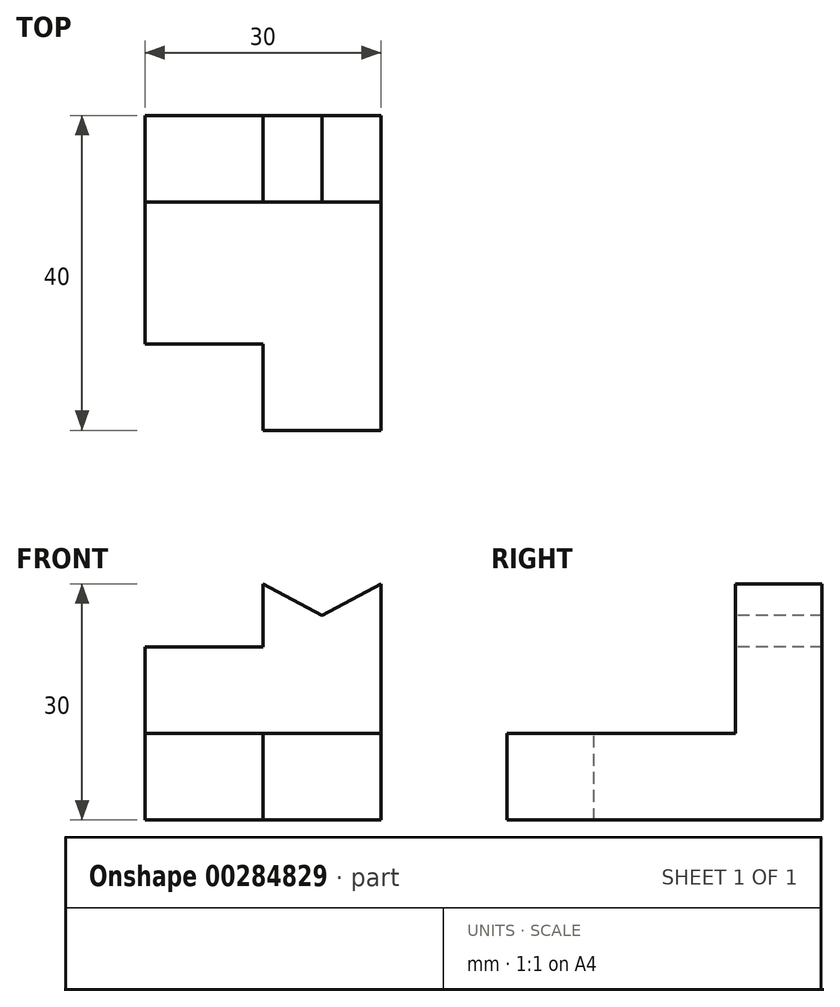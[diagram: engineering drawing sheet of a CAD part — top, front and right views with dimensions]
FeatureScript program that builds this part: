
annotation { "Feature Type Name" : "Feature", "Feature Type Description" : "" }
export const myFeature = defineFeature(function(context is Context, id is Id, definition is map)
    precondition{}
    {
        {
            var Q0;
            Q0=qCreatedBy(makeId("Front.planeOp"),FACE);
            var sketch = newSketch(context, id + "F0", { "sketchPlane" : qUnion([Q0])});
            skLineSegment(sketch, "E0.bottom", {"start": v(0, 0) * mm, "end": v(40, 0) * mm});
            skLineSegment(sketch, "E0.top", {"start": v(0, 30) * mm, "end": v(40, 30) * mm});
            skLineSegment(sketch, "E0.left", {"start": v(0, 0) * mm, "end": v(0, 30) * mm});
            skLineSegment(sketch, "E0.right", {"start": v(40, 0) * mm, "end": v(40, 30) * mm});
            skLineSegment(sketch, "E1.bottom", {"start": v(40, 30) * mm, "end": v(11, 30) * mm});
            skLineSegment(sketch, "E1.top", {"start": v(40, 11) * mm, "end": v(11, 11) * mm});
            skLineSegment(sketch, "E1.left", {"start": v(40, 30) * mm, "end": v(40, 11) * mm});
            skLineSegment(sketch, "E1.right", {"start": v(11, 30) * mm, "end": v(11, 11) * mm});
            skSolve(sketch);
        }
        {
            var Q0;
            Q0=makeQuery(id+"F0.imprint","IMPRINT",FACE,{"disambiguationData":[TD([[makeQuery(id+"F0.imprint","IMPRINT",EDGE,{"derivedFrom":sQuery(id+"F0.wireOp",EDGE,"E0.bottom")}),1.0]])]});
            extrude(context, id + "F1", {"entities" : qUnion([Q0]), "depth" : 30 * mm});
        }
        {
            var Q0;
            Q0=makeQuery(id+"F1.opExtrude","SWEPT_FACE",FACE,{"disambiguationData":[OSD([sQuery(id+"F0.wireOp",EDGE,"E1.top")])]});
            var sketch = newSketch(context, id + "F2", { "sketchPlane" : qUnion([Q0])});
            skPoint(sketch, "E2.oppositeSnap0", {"position": v(40, -15) * mm});
            skLineSegment(sketch, "E2.bottom", {"start": v(40, -30) * mm, "end": v(29, -30) * mm});
            skLineSegment(sketch, "E2.top", {"start": v(40, -15) * mm, "end": v(29, -15) * mm});
            skLineSegment(sketch, "E2.left", {"start": v(40, -30) * mm, "end": v(40, -15) * mm});
            skLineSegment(sketch, "E2.right", {"start": v(29, -30) * mm, "end": v(29, -15) * mm});
            skSolve(sketch);
        }
        {
            var Q0;
            Q0=qSketchRegion(id+"F2",true);
            var Q1;
            Q1=makeQuery(id+"F1.opExtrude","CAP_VERTEX",VERTEX,{"disambiguationData":[OSD([sQuery(id+"F0.wireOp",EDGE,"E0.bottom"),sQuery(id+"F0.wireOp",EDGE,"E0.right")])],"isStart":false});
            extrude(context, id + "F3", {"entities" : qUnion([Q0]), "operationType" : NewBodyOperationType.REMOVE, "endBound" : BoundingType.UP_TO_VERTEX, "oppositeDirection" : true, "endBoundEntityVertex" : qUnion([Q1]), "depth" : 25 * mm});
        }
        {
            var Q0;
            Q0=makeQuery(id+"F1.opExtrude","SWEPT_FACE",FACE,{"disambiguationData":[OSD([sQuery(id+"F0.wireOp",EDGE,"E1.right")])]});
            var sketch = newSketch(context, id + "F4", { "sketchPlane" : qUnion([Q0])});
            skPoint(sketch, "E3.oppositeSnap0", {"position": v(-15, 30) * mm});
            skLineSegment(sketch, "E3.bottom", {"start": v(-30, 30) * mm, "end": v(-15, 30) * mm});
            skLineSegment(sketch, "E3.top", {"start": v(-30, 22) * mm, "end": v(-15, 22) * mm});
            skLineSegment(sketch, "E3.left", {"start": v(-30, 30) * mm, "end": v(-30, 22) * mm});
            skLineSegment(sketch, "E3.right", {"start": v(-15, 30) * mm, "end": v(-15, 22) * mm});
            skSolve(sketch);
        }
        {
            var Q0;
            Q0=qSketchRegion(id+"F4",true);
            var Q1;
            Q1=makeQuery(id+"F1.opExtrude","CAP_VERTEX",VERTEX,{"disambiguationData":[OSD([sQuery(id+"F0.wireOp",EDGE,"E0.top"),sQuery(id+"F0.wireOp",EDGE,"E0.left")])],"isStart":false});
            extrude(context, id + "F5", {"entities" : qUnion([Q0]), "operationType" : NewBodyOperationType.REMOVE, "endBound" : BoundingType.UP_TO_VERTEX, "oppositeDirection" : true, "endBoundEntityVertex" : qUnion([Q1]), "depth" : 25 * mm});
        }
        {
            var Q0;
            Q0=makeQuery(id+"F1.opExtrude","SWEPT_BODY",BODY,{"disambiguationData":[OSD([sQuery(id+"F0.wireOp",EDGE,"E0.bottom"),sQuery(id+"F0.wireOp",EDGE,"E0.top"),sQuery(id+"F0.wireOp",EDGE,"E0.left"),sQuery(id+"F0.wireOp",EDGE,"E0.right"),sQuery(id+"F0.wireOp",EDGE,"E1.top"),sQuery(id+"F0.wireOp",EDGE,"E1.right")])]});
            var Q1;
            Q1=makeQuery(id+"F1.opExtrude","CAP_EDGE",EDGE,{"disambiguationData":[OSD([sQuery(id+"F0.wireOp",EDGE,"E0.left")])],"isStart":true});
            transform(context, id + "F6", {"entities" : qUnion([Q0]), "transformType" : TransformType.ROTATION, "transformAxis" : qUnion([Q1]), "angle" : 90 * degree, "oppositeDirection" : true, "makeCopy" : false});
        }
        {
            var Q0;
            Q0=makeQuery(id+"F1.opExtrude","SWEPT_FACE",FACE,{"disambiguationData":[OSD([sQuery(id+"F0.wireOp",EDGE,"E1.right")])]});
            var sketch = newSketch(context, id + "F7", { "sketchPlane" : qUnion([Q0])});
            skLineSegment(sketch, "E4", {"start": v(-15, 30) * mm, "end": v(0, 22) * mm});
            skLineSegment(sketch, "E5", {"start": v(-15, 22) * mm, "end": v(0, 30) * mm});
            skSolve(sketch);
        }
        {
            var Q0;
            {var subQ1=makeQuery(id+"F5.boolean.opBoolean","COPY",EDGE,{"derivedFrom":makeQuery(id+"F5.opExtrude","CAP_EDGE",EDGE,{"disambiguationData":[OSD([sQuery(id+"F4.wireOp",EDGE,"E3.right")])],"isStart":true})});Q0=makeQuery(id+"F7.imprint","IMPRINT",FACE,{"disambiguationData":[TD([[makeQuery(id+"F7.imprint","IMPRINT",EDGE,{"derivedFrom":subQ1}),1.0]])]});}
            var Q1;
            {var subQ1=sQuery(id+"F0.wireOp",EDGE,"E1.right");var subQ2=makeQuery(id+"F1.opExtrude","SWEPT_EDGE",EDGE,{"disambiguationData":[OSD([sQuery(id+"F0.wireOp",EDGE,"E0.top"),sQuery(id+"F0.wireOp",EDGE,"E1.bottom"),subQ1])]});Q1=makeQuery(id+"F7.imprint","IMPRINT",FACE,{"disambiguationData":[TD([[makeQuery(id+"F7.imprint","IMPRINT",EDGE,{"derivedFrom":subQ2}),-1.0]])]});}
            extrude(context, id + "F8", {"entities" : qUnion([Q0, Q1]), "operationType" : NewBodyOperationType.REMOVE, "endBound" : BoundingType.THROUGH_ALL, "oppositeDirection" : true, "depth" : 25 * mm});
        }
    });
